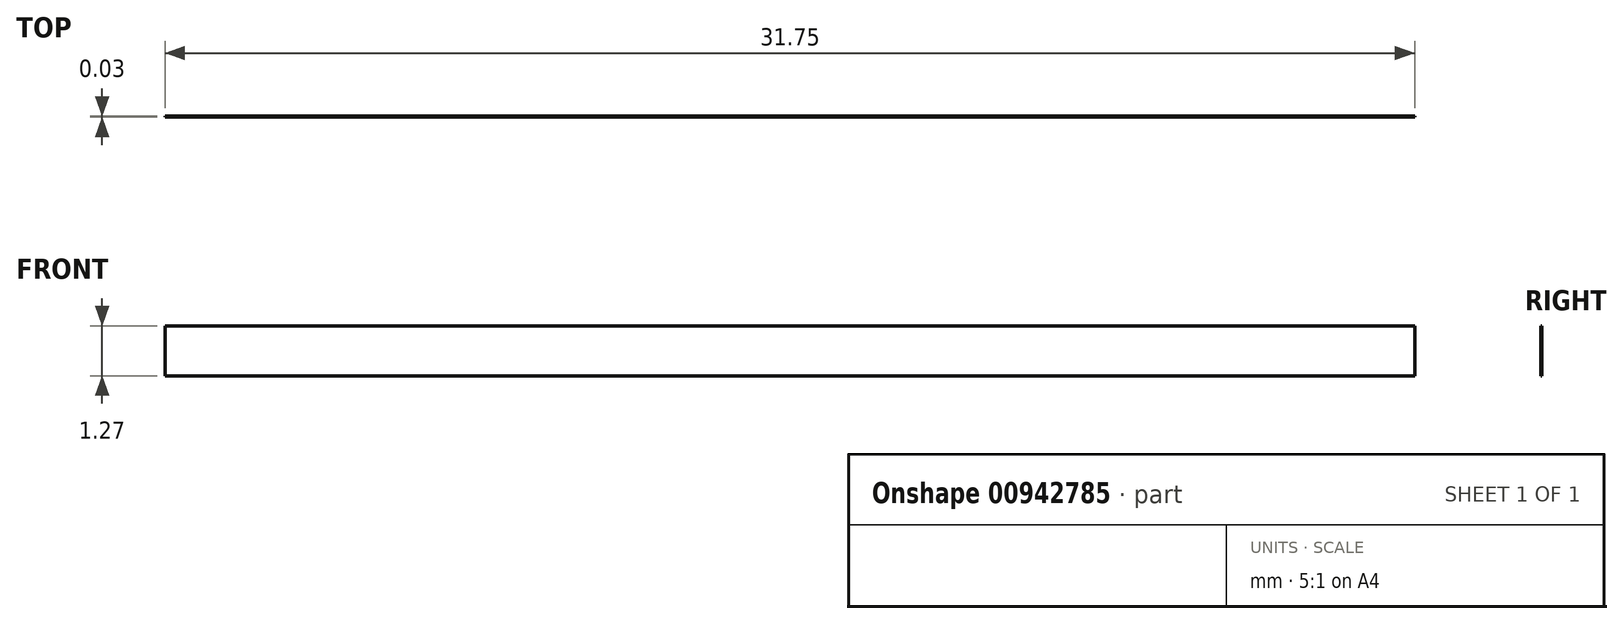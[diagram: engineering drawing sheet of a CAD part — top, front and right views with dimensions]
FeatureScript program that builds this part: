
annotation { "Feature Type Name" : "Feature", "Feature Type Description" : "" }
export const myFeature = defineFeature(function(context is Context, id is Id, definition is map)
    precondition{}
    {
        {
            var Q0;
            Q0=qCreatedBy(makeId("Front.planeOp"),FACE);
            var sketch = newSketch(context, id + "F0", { "sketchPlane" : qUnion([Q0])});
            skLineSegment(sketch, "E0.bottom", {"start": v(0, 0) * mm, "end": v(31.75, 0) * mm});
            skLineSegment(sketch, "E0.top", {"start": v(0, 1.27) * mm, "end": v(31.75, 1.27) * mm});
            skLineSegment(sketch, "E0.left", {"start": v(0, 0) * mm, "end": v(0, 1.27) * mm});
            skLineSegment(sketch, "E0.right", {"start": v(31.75, 0) * mm, "end": v(31.75, 1.27) * mm});
            skSolve(sketch);
        }
        {
            var Q0;
            Q0=makeQuery(id+"F0.imprint","IMPRINT",FACE,{"disambiguationData":[TD([[makeQuery(id+"F0.imprint","IMPRINT",EDGE,{"derivedFrom":sQuery(id+"F0.wireOp",EDGE,"E0.bottom")}),1.0]])]});
            extrude(context, id + "F1", {"entities" : qUnion([Q0]), "depth" : 0.03 * mm, "offsetDistance" : 25.4 * mm});
        }
    });
